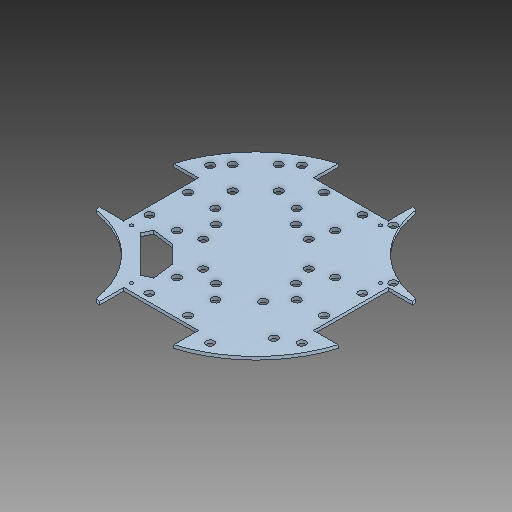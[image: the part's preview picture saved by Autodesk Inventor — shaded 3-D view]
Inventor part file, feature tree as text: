
AUTODESK INVENTOR PART (.ipt)
format: ipt  version: 2020 (Build 240168000, 168)  size: 458,240 bytes
history: native  units: mm
features: sketch x8, extrude x6, hole x2, projected_geometry x2, other x1
ambient origin geometry x8: Origin, YZ Plane, XZ Plane, XY Plane, X Axis, Y Axis, Z Axis, Center Point
bodies: Body1 (feature_tree)
feature tree (19):
  other  "Твердое тело1"
  extrude  "Выдавливание1"  Depth=2.66mm TaperAngle=0.0deg
  extrude  "Выдавливание2"  Depth=6.6mm
  extrude  "Выдавливание3"  Depth=2.66mm TaperAngle=0.0deg
  sketch  "Эскиз7"
  extrude  "Выдавливание6"  Depth=13.0mm
  extrude  "Выдавливание7"  Depth=13.0mm
  extrude  "Выдавливание8"  Depth=13.0mm
  hole  "Отверстие1"  [1 undecoded]
  hole  "Отверстие2"  [1 undecoded]
  sketch  "Эскиз3"
  sketch  "Эскиз5"
  projected_geometry  "Спроецированная петля1"
  projected_geometry  "Спроецированная петля2"
  sketch  "Эскиз9"
  sketch  "Эскиз11"
  sketch  "Эскиз12"
  sketch  "Эскиз13"
  sketch  "Эскиз14"
note: 2 required parameter values undecoded (feature->parameter linkage not recoverable at this tier; creation-order binding heuristic only, values carry confidence <= 0.55)
